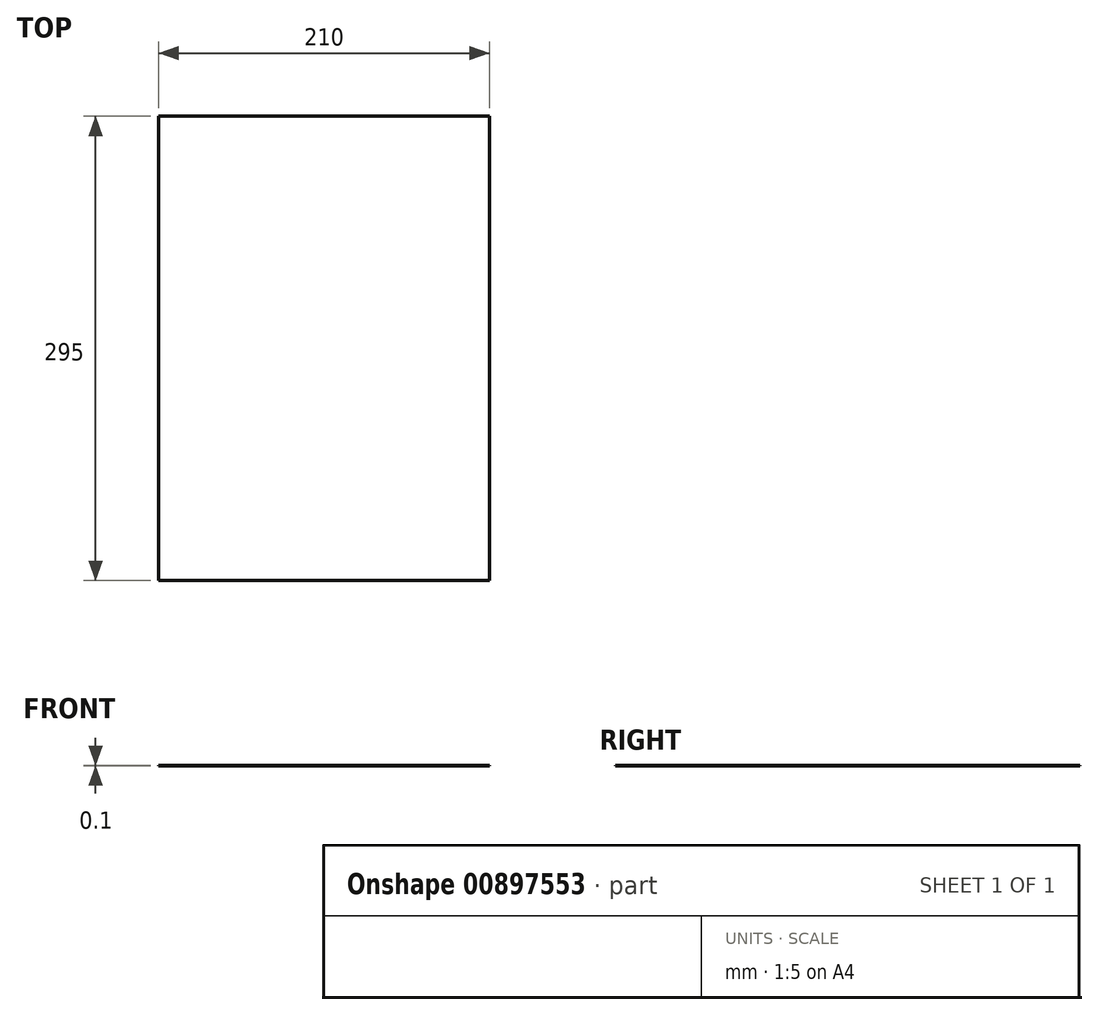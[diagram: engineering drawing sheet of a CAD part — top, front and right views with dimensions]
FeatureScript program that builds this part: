
annotation { "Feature Type Name" : "Feature", "Feature Type Description" : "" }
export const myFeature = defineFeature(function(context is Context, id is Id, definition is map)
    precondition{}
    {
        {
            var Q0;
            Q0=qCreatedBy(makeId("Top.planeOp"),FACE);
            var sketch = newSketch(context, id + "F0", { "sketchPlane" : qUnion([Q0])});
            skLineSegment(sketch, "E0.bottom", {"start": v(-21.8, 270) * mm, "end": v(188.2, 270) * mm});
            skLineSegment(sketch, "E0.top", {"start": v(-21.8, -25) * mm, "end": v(188.2, -25) * mm});
            skLineSegment(sketch, "E0.left", {"start": v(-21.8, 270) * mm, "end": v(-21.8, -25) * mm});
            skLineSegment(sketch, "E0.right", {"start": v(188.2, 270) * mm, "end": v(188.2, -25) * mm});
            skSolve(sketch);
        }
        {
            var Q0;
            Q0 = qSketchRegion(id + "F0", true);
            extrude(context, id + "F1", {"entities" : qUnion([Q0]), "depth" : 0.1 * mm, "offsetDistance" : 25 * mm});
        }
    });
